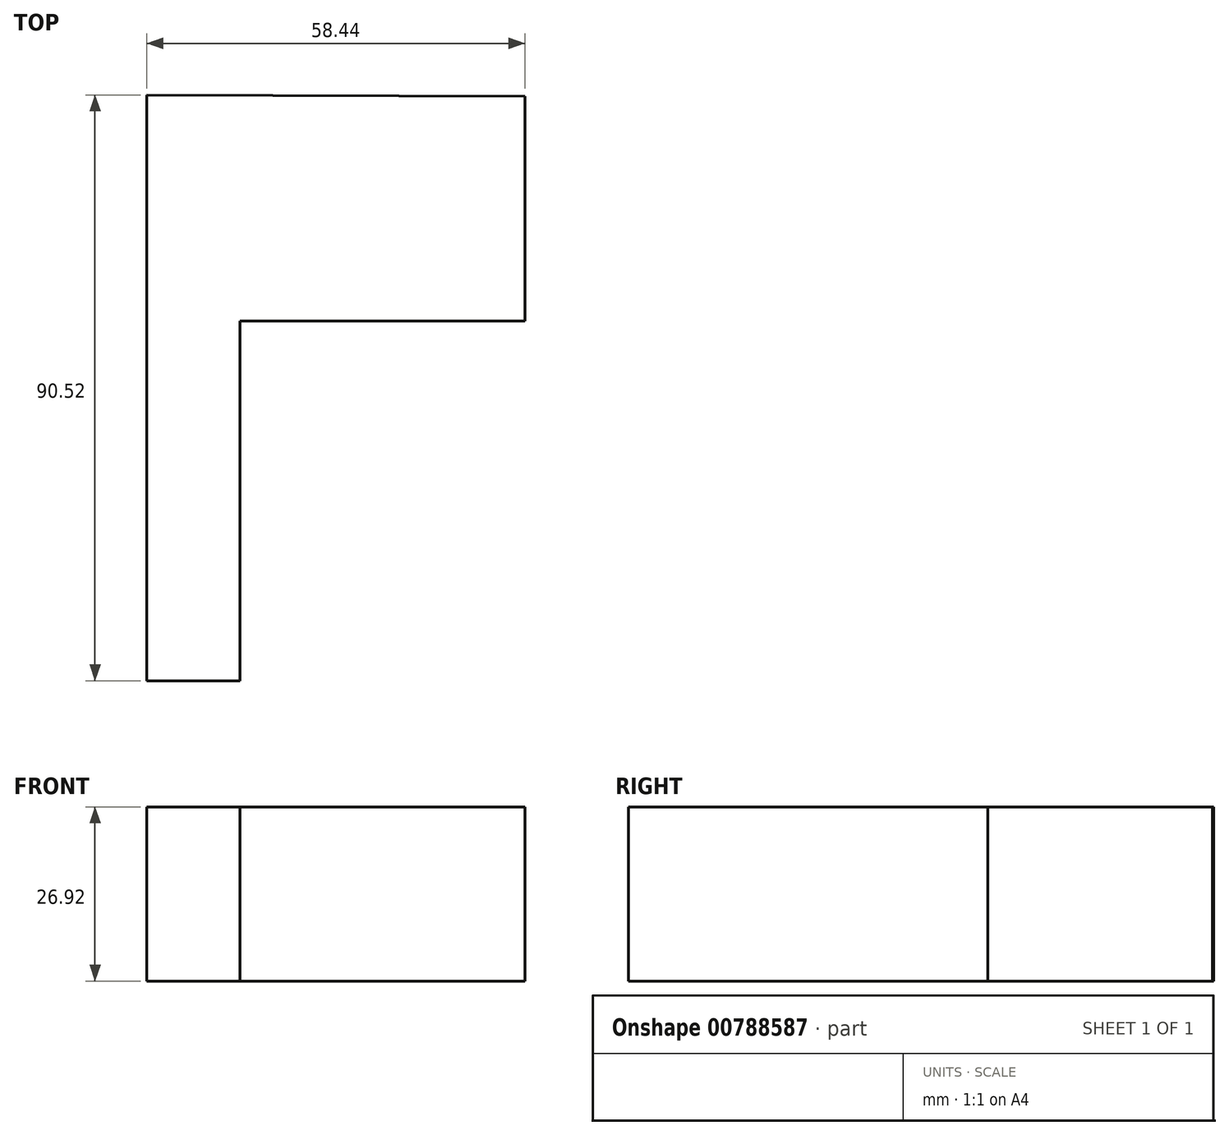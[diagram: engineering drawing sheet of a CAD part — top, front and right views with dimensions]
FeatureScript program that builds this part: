
annotation { "Feature Type Name" : "Feature", "Feature Type Description" : "" }
export const myFeature = defineFeature(function(context is Context, id is Id, definition is map)
    precondition{}
    {
        {
            var Q0;
            Q0=qCreatedBy(makeId("Top.planeOp"),FACE);
            var sketch = newSketch(context, id + "F0", { "sketchPlane" : qUnion([Q0])});
            skLineSegment(sketch, "E0", {"start": v(-30.14, 34.94) * mm, "end": v(-30.14, -55.58) * mm});
            skLineSegment(sketch, "E1", {"start": v(-30.14, -55.58) * mm, "end": v(-15.76, -55.58) * mm});
            skLineSegment(sketch, "E2", {"start": v(-15.76, -55.58) * mm, "end": v(-15.76, 0) * mm});
            skLineSegment(sketch, "E3", {"start": v(-15.76, 0) * mm, "end": v(28.3, 0) * mm});
            skLineSegment(sketch, "E4", {"start": v(28.3, 0) * mm, "end": v(28.3, 34.75) * mm});
            skLineSegment(sketch, "E5", {"start": v(28.3, 34.75) * mm, "end": v(-30.14, 34.94) * mm});
            skSolve(sketch);
        }
        {
            var Q0;
            Q0 = qSketchRegion(id + "F0", true);
            extrude(context, id + "F1", {"entities" : qUnion([Q0]), "depth" : 26.92 * mm, "offsetDistance" : 25.4 * mm});
        }
        {
            var Q0;
            Q0=makeQuery(id+"F1.opExtrude","CAP_FACE",FACE,{"disambiguationData":[OSD([sQuery(id+"F0.wireOp",EDGE,"E0"),sQuery(id+"F0.wireOp",EDGE,"E1"),sQuery(id+"F0.wireOp",EDGE,"E2"),sQuery(id+"F0.wireOp",EDGE,"E3"),sQuery(id+"F0.wireOp",EDGE,"E4"),sQuery(id+"F0.wireOp",EDGE,"E5")])],"isStart":false});
            var sketch = newSketch(context, id + "F2", { "sketchPlane" : qUnion([Q0])});
            skLineSegment(sketch, "E6.bottom", {"start": v(-14.29, 24.06) * mm, "end": v(18.9, 24.06) * mm});
            skLineSegment(sketch, "E6.top", {"start": v(-14.29, 8.39) * mm, "end": v(18.9, 8.39) * mm});
            skLineSegment(sketch, "E6.left", {"start": v(-14.29, 24.06) * mm, "end": v(-14.29, 8.39) * mm});
            skLineSegment(sketch, "E6.right", {"start": v(18.9, 24.06) * mm, "end": v(18.9, 8.39) * mm});
            skSolve(sketch);
        }
        {
            var Q0;
            Q0 = qSketchRegion(id + "F2", true);
            extrude(context, id + "F3", {"entities" : qUnion([Q0]), "operationType" : NewBodyOperationType.ADD, "oppositeDirection" : true, "depth" : 10.92 * mm, "offsetDistance" : 25.4 * mm});
        }
    });
